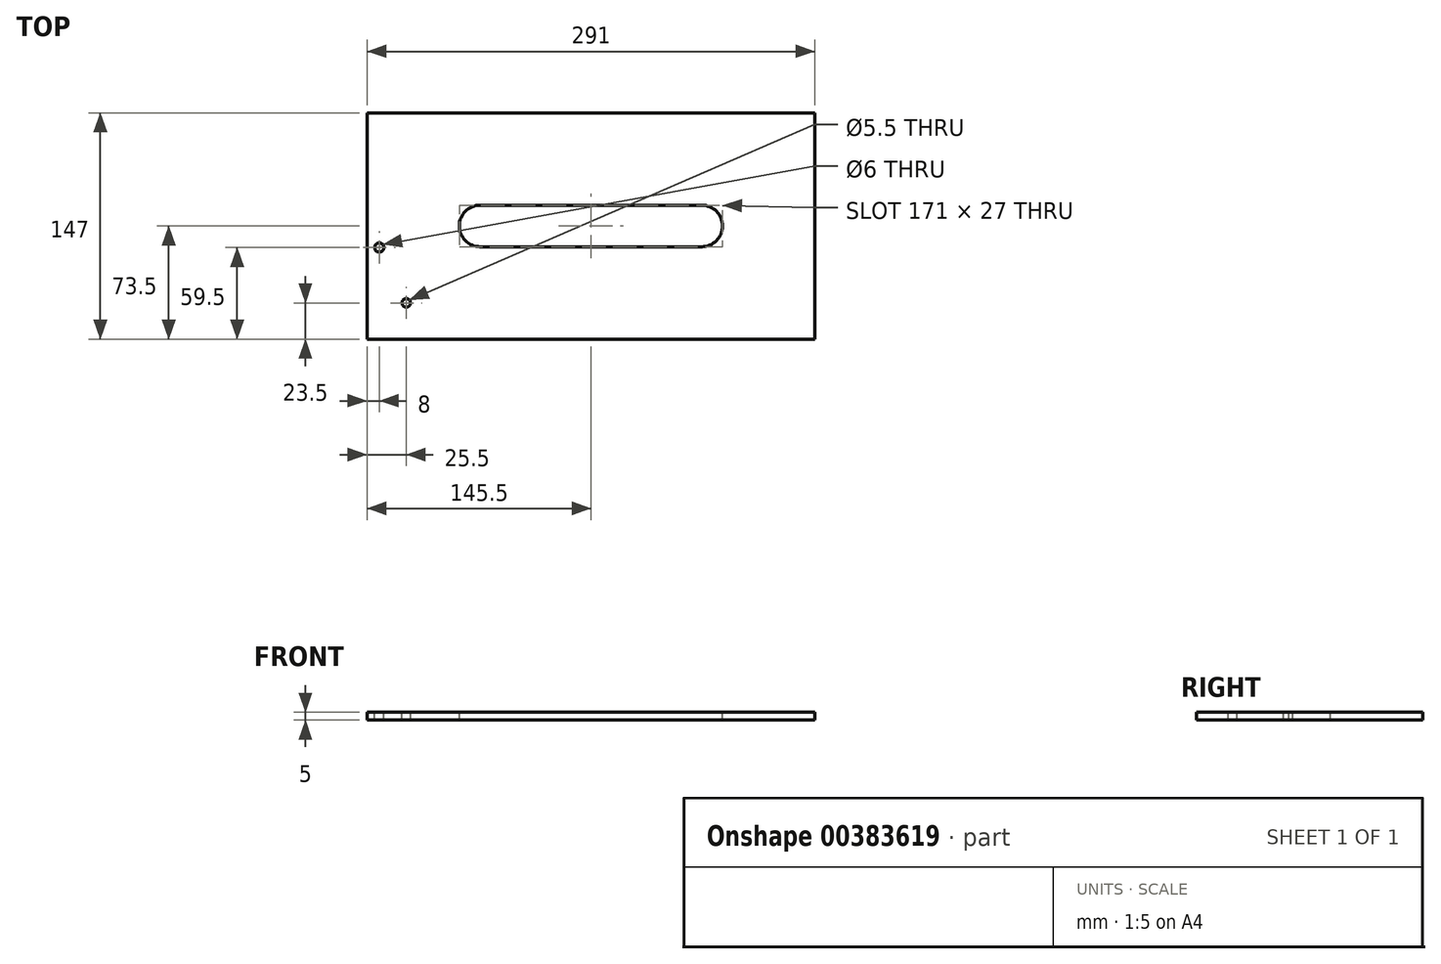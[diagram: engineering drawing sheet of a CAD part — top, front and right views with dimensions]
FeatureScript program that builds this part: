
annotation { "Feature Type Name" : "Feature", "Feature Type Description" : "" }
export const myFeature = defineFeature(function(context is Context, id is Id, definition is map)
    precondition{}
    {
        {
            var Q0;
            Q0=qCreatedBy(makeId("Top.planeOp"),FACE);
            var sketch = newSketch(context, id + "F0", { "sketchPlane" : qUnion([Q0])});
            skLineSegment(sketch, "E0.bottom", {"start": v(-72, -8) * mm, "end": v(72, -8) * mm});
            skLineSegment(sketch, "E0.top", {"start": v(-72, 8) * mm, "end": v(72, 8) * mm});
            skArc(sketch, "E1", {"start": v(-72, 8) * mm, "mid": v(-80, 0) * mm, "end": v(-72, -8) * mm});
            skArc(sketch, "E2", {"start": v(72, -8) * mm, "mid": v(80, 0) * mm, "end": v(72, 8) * mm});
            skLineSegment(sketch, "E3", {"start": v(-177.56, -17) * mm, "end": v(188.12, -17) * mm});
            skSolve(sketch);
        }
        {
            var Q0;
            Q0=qCreatedBy(makeId("Top.planeOp"),FACE);
            var sketch = newSketch(context, id + "F1", { "sketchPlane" : qUnion([Q0])});
            skCircle(sketch, "E4", {"center": v(-46.96, -4) * mm, "radius": 4 * mm});
            skCircle(sketch, "E5", {"center": v(-46.96, -4) * mm, "radius": 9.5 * mm, "construction": true});
            skSolve(sketch);
        }
        {
            var Q0;
            Q0=qCreatedBy(makeId("Top.planeOp"),FACE);
            var sketch = newSketch(context, id + "F2", { "sketchPlane" : qUnion([Q0])});
            skLineSegment(sketch, "E6.bottom", {"start": v(-72, 13.5) * mm, "end": v(72, 13.5) * mm});
            skLineSegment(sketch, "E6.top", {"start": v(-72, -13.5) * mm, "end": v(72, -13.5) * mm});
            skArc(sketch, "E7", {"start": v(-72, 13.5) * mm, "mid": v(-85.5, 0) * mm, "end": v(-72, -13.5) * mm});
            skArc(sketch, "E8", {"start": v(72, -13.5) * mm, "mid": v(85.5, 0) * mm, "end": v(72, 13.5) * mm});
            skLineSegment(sketch, "E9.bottom", {"start": v(-145.5, 73.5) * mm, "end": v(145.5, 73.5) * mm});
            skLineSegment(sketch, "E9.top", {"start": v(-145.5, -73.5) * mm, "end": v(145.5, -73.5) * mm});
            skLineSegment(sketch, "E9.left", {"start": v(-145.5, 73.5) * mm, "end": v(-145.5, -73.5) * mm});
            skLineSegment(sketch, "E9.right", {"start": v(145.5, 73.5) * mm, "end": v(145.5, -73.5) * mm});
            skSolve(sketch);
        }
        {
            var Q0;
            Q0=makeQuery(id+"F2.imprint","IMPRINT",FACE,{"disambiguationData":[TD([[makeQuery(id+"F2.imprint","IMPRINT",EDGE,{"derivedFrom":sQuery(id+"F2.wireOp",EDGE,"E6.bottom")}),1.0]])]});
            extrude(context, id + "F3", {"entities" : qUnion([Q0]), "oppositeDirection" : true, "depth" : 5 * mm});
        }
        {
            var Q0;
            Q0=qCreatedBy(makeId("Top.planeOp"),FACE);
            var sketch = newSketch(context, id + "F4", { "sketchPlane" : qUnion([Q0])});
            skPoint(sketch, "E10", {"position": v(-120, -50) * mm});
            skSolve(sketch);
        }
        {
            var Q0;
            Q0=sQuery(id+"F4.wireOp",VERTEX,"E10");
            var Q1;
            Q1=makeQuery(id+"F3.opExtrude","SWEPT_BODY",BODY,{"disambiguationData":[OSD([sQuery(id+"F2.wireOp",EDGE,"E6.bottom"),sQuery(id+"F2.wireOp",EDGE,"E6.top"),sQuery(id+"F2.wireOp",EDGE,"E7"),sQuery(id+"F2.wireOp",EDGE,"E8"),sQuery(id+"F2.wireOp",EDGE,"E9.bottom"),sQuery(id+"F2.wireOp",EDGE,"E9.top"),sQuery(id+"F2.wireOp",EDGE,"E9.left"),sQuery(id+"F2.wireOp",EDGE,"E9.right")])]});
            hole(context, id + "F5", {"style" : HoleStyle.SIMPLE, "endStyle" : HoleEndStyle.THROUGH, "standardTappedOrClearance" : lookupTablePath({ "standard" : "ISO", "fit" : "Normal", "size" : "M5", "type" : "Clearance" }), "standardBlindInLast" : lookupTablePath({ "fit" : "Standard", "standard" : "ISO", "size" : "M5", "type" : "Clearance" }), "holeDiameter" : 5.5 * mm, "isTappedThrough" : true, "tappedDepth" : 12 * mm, "tapClearance" : 3, "locations" : qUnion([Q0]), "scope" : qUnion([Q1])});
        }
        {
            var Q0;
            Q0=qCreatedBy(makeId("Top.planeOp"),FACE);
            var sketch = newSketch(context, id + "F6", { "sketchPlane" : qUnion([Q0])});
            skCircle(sketch, "E11", {"center": v(-137.5, -14) * mm, "radius": 3 * mm});
            skSolve(sketch);
        }
        {
            var Q0;
            Q0=makeQuery(id+"F6.imprint","IMPRINT",FACE,{"disambiguationData":[TD([[makeQuery(id+"F6.imprint","IMPRINT",EDGE,{"derivedFrom":sQuery(id+"F6.wireOp",EDGE,"E11")}),1.0]])]});
            extrude(context, id + "F7", {"entities" : qUnion([Q0]), "operationType" : NewBodyOperationType.REMOVE, "endBound" : BoundingType.THROUGH_ALL, "oppositeDirection" : true, "depth" : 25 * mm});
        }
    });
